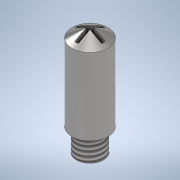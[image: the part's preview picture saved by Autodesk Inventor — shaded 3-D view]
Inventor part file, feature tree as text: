
AUTODESK INVENTOR PART (.ipt)
format: ipt  version: 2020 (Build 240168000, 168)  size: 173,568 bytes
history: native  units: mm
features: extrude x4, sketch x4, thread x1
ambient origin geometry x8: Origin, YZ Plane, XZ Plane, XY Plane, X Axis, Y Axis, Z Axis, Center Point
bodies: Solid1 (feature_tree)
feature tree (9):
  extrude  "Extrusion1"  Depth=2.5mm TaperAngle=0.0deg
  extrude  "Extrusion2"  Depth=8.5mm TaperAngle=0.0deg
  thread  "Thread1"  [1 undecoded]
  extrude  "Extrusion3"  Depth=1.0mm
  extrude  "Extrusion4"  Depth=0.05mm
  sketch  "Sketch1"  dims[d0=3.0mm d1=2.5mm d2=0.0mm]
  sketch  "Sketch2"  dims[d3=4.0mm d4=8.5mm d5=0.0mm d6=5.5mm d7=0.0mm]
  sketch  "Sketch3"  dims[d8=4.0mm d9=1.0mm d10=-10.471976mm]
  sketch  "Sketch4"  dims[d11=0.4mm d12=3.0mm d13=3.0mm d14=0.4mm d15=0.05mm d16=0.05mm d17=0.05mm d18=1.0mm d19=0.0mm]
note: 1 required parameter value undecoded (feature->parameter linkage not recoverable at this tier; creation-order binding heuristic only, values carry confidence <= 0.55)
